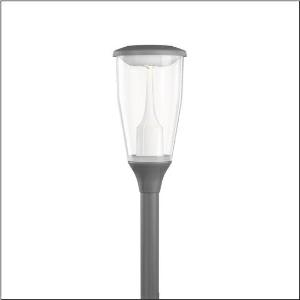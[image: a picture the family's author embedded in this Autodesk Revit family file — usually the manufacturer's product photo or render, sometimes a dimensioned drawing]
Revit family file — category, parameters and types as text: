
# Revit family: dl_11_iq___st1_2a_5xa5575mf14hp00022_5a95
name_source: partatom
category: Lighting Fixtures
units: mm (PartAtom-declared; Revit-internal decimal feet)

## family parameters
Cut with Voids When Loaded = No
Host = Face
Light Source = No
Part Type = Normal
Room Calculation Point = No
Round Connector Dimension = Use Diameter
Shared = No

## types (1)
- --- (1 x LED, 4340 lm, 33.6 W, 2700K)
    Apparent Load = 34 VA
    CIE Flux Codes = 33 63 91 94 100
    Color Rendering = 70
    Color Temperature = 2700K
    Default Elevation = 1800 mm
    Description = DL 11 iQ, mast luminaire, Module 540 iQ-SR, primary light control with 3 zone facetted reflector, of plastic, silver coated, highly specular, structured, primary optical cover: cover, of PMMA, transparent, light distribution: ST1.2a, light emission: direct distribution, primary light characteristic: asymmetric, installation type: post-top, LED, High Power LED, light colour: 727, colour temperature: 2700K, control: Street-Remote, Auto-Match, Temp-Guard, Lumen-Switch, Night-Set, Smart-Wire, Light-Fading, Desk-Remote (wireless, voltage-free reading and setting of iQ features in the workshop via application-optimized NFC function/RFID function), optimised constant luminous flux control (CLO 2.0), mains connection: 220..240V, AC, 50/60Hz, connection cable pre-assembled, cable length: 5,5m, wiring characteristics: H07RN-F, 5-core, 1.5mm², start of lifetime: 34W, end of service life: 36W, luminaire housing, upper part, of diecast aluminium, coated, Siteco® metallic grey (DB 702S), spigot size: 76mm (post-top), post-top mast mounting element, of diecast aluminium, coated, Siteco® metallic grey (DB 702S), Module 540 iQ-SR, traffic white (RAL 9016), equipment: Power, protection rating (complete): IP66, insulation class (complete): insulation class II (safety insulation), certification: CE, ENEC, ENEC+, VDE, packaging unit: 1 piece

Light Distribution: ST1.2a
    Height = 665 mm
    Lamp = 1 x LED
    Lamp Light Flux = 4340 lm
    Lamp Power = 33.6 W
    Lamp count = 1
    Length = 334 mm
    Luminous efficacy = 129 lm/W
    Manufacturer = Siteco
    ModVariant = No
    Model = 5XA5575MF14HP00022
    Number of Poles = 1
    OnlyDefault = Yes
    Power Factor = 1
    Product Name = DL 11 iQ | ST1.2a
    Product group = mast luminaire | pylon top
    ProductGroupID = 6100
    Protection Class = Protection class II
    Protection Degree = IP 66
    RLX_Detail_Level = 1
    RLX_Emergency_Light_Flux = 0 lm
    RLX_Emergency_Type = 0
    RLX_Emergency_Type_DB = No
    RlxData = <blob elided: 98413 chars, md5=10ed600b>
    Socket = socket
    Standby Power = 0 W
    System Light Flux = 4340 lm
    System Power = 34 W
    Type Comments = factory setting: luminous flux: 100 % | dim-lin: 254 | 695 mA
    Type Image = l_1258354.jpg
    URL = http://relux.com
    VarID = @adj_002461
    Voltage = 0 V
    Weight = 0.00 kg
    Width = 0 mm  [stored 0 ft]

note: [stored X ft] marks values corroborated as IEEE doubles in the binary element streams (Revit-internal decimal feet)

## geometry (parser evidence)
native form markers: Blend x4, Sweep x13
no freeform markers — native parametric forms only
